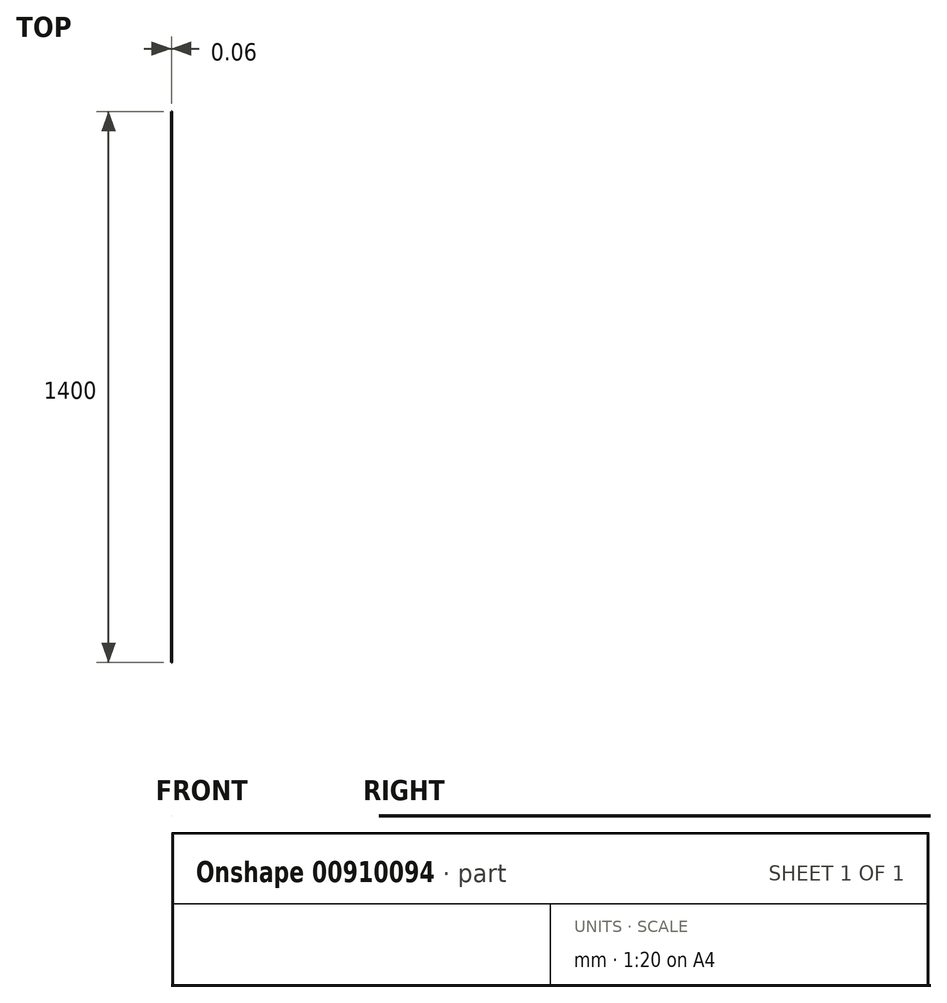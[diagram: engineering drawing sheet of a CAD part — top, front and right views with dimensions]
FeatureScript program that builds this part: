
annotation { "Feature Type Name" : "Feature", "Feature Type Description" : "" }
export const myFeature = defineFeature(function(context is Context, id is Id, definition is map)
    precondition{}
    {
        {
            var Q0;
            Q0=qCreatedBy(makeId("Front.planeOp"),FACE);
            var sketch = newSketch(context, id + "F0", { "sketchPlane" : qUnion([Q0])});
            skArc(sketch, "E0", {"start": v(-102.93, -1.58) * mm, "mid": v(-101.66, -2.81) * mm, "end": v(-99.94, -3.26) * mm});
            skLineSegment(sketch, "E1", {"start": v(-52.25, -3.26) * mm, "end": v(-99.94, -3.26) * mm});
            skArc(sketch, "E2", {"start": v(-52.31, -3.26) * mm, "mid": v(-50.61, -2.84) * mm, "end": v(-49.33, -1.64) * mm});
            skArc(sketch, "E3", {"start": v(-49.37, -1.7) * mm, "mid": v(-46.94, 3.56) * mm, "end": v(-46.11, 9.3) * mm});
            skArc(sketch, "E4", {"start": v(-106.11, 9.29) * mm, "mid": v(-105.28, 3.52) * mm, "end": v(-102.82, -1.75) * mm});
            skLineSegment(sketch, "E5", {"start": v(-46.11, 9.29) * mm, "end": v(-16.11, 9.29) * mm});
            skLineSegment(sketch, "E6", {"start": v(-16.11, 9.29) * mm, "end": v(-16.11, -30.71) * mm});
            skLineSegment(sketch, "E7", {"start": v(-16.11, -30.71) * mm, "end": v(-136.11, -30.71) * mm});
            skLineSegment(sketch, "E8", {"start": v(-136.11, -30.71) * mm, "end": v(-136.11, 9.29) * mm});
            skLineSegment(sketch, "E9", {"start": v(-136.11, 9.29) * mm, "end": v(-106.11, 9.29) * mm});
            skSolve(sketch);
        }
        {
            var Q0;
            {var subQ9=sQuery(id+"F0.wireOp",EDGE,"E1");Q0=makeQuery(id+"F0.imprint","IMPRINT",FACE,{"disambiguationData":[TD([[makeQuery(id+"F0.imprint","IMPRINT",EDGE,{"derivedFrom":subQ9}),1.0]])]});}
            extrude(context, id + "F1", {"entities" : qUnion([Q0]), "depth" : 1400 * mm, "offsetDistance" : 25 * mm});
        }
    });
